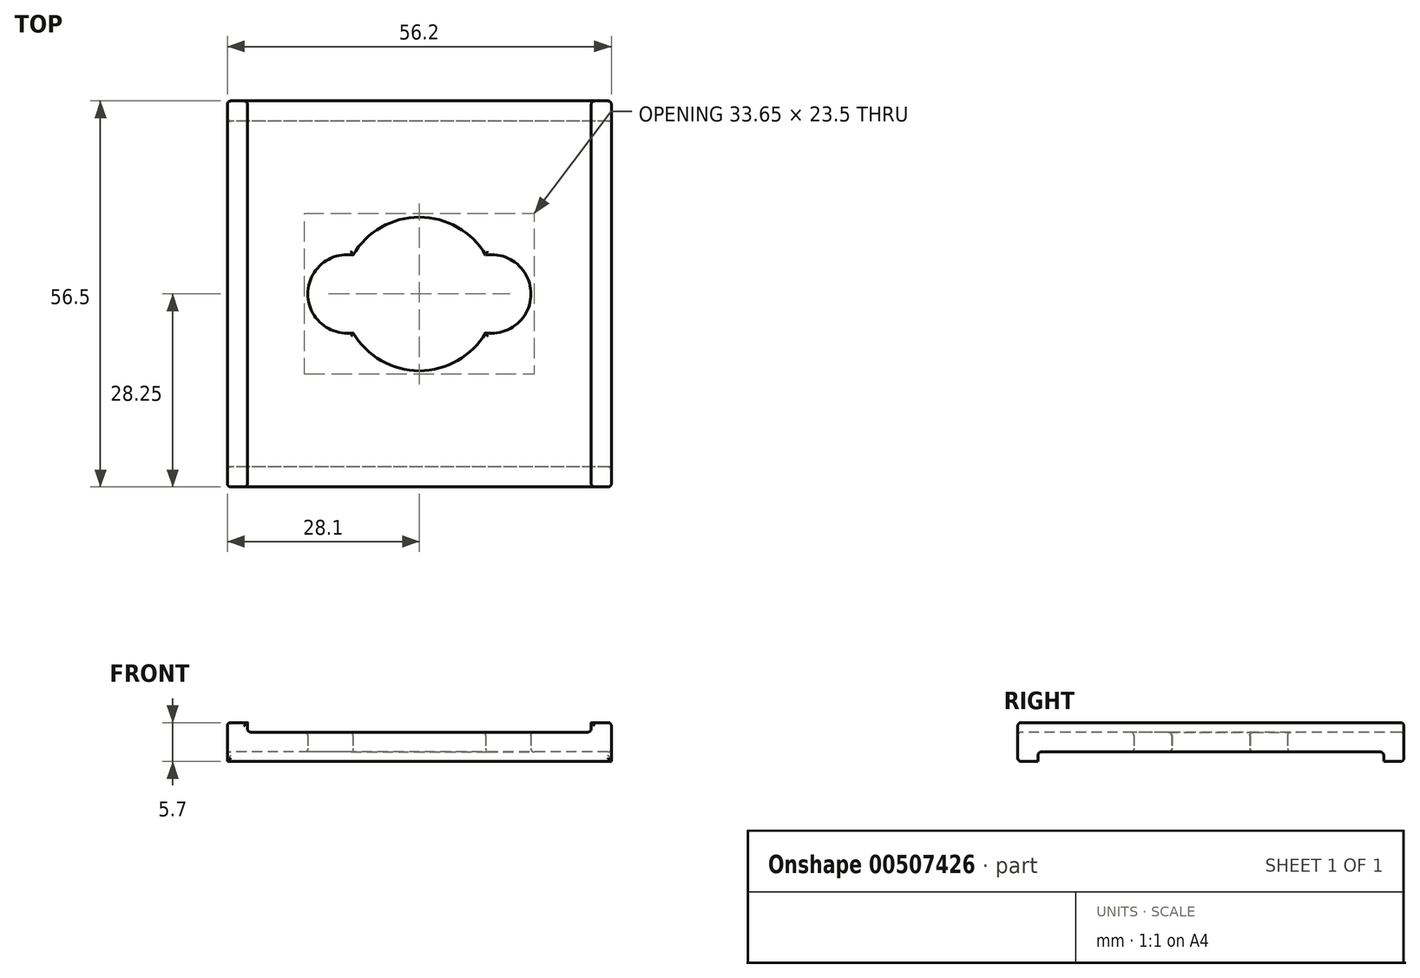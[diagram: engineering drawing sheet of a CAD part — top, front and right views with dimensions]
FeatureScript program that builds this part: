
annotation { "Feature Type Name" : "Feature", "Feature Type Description" : "" }
export const myFeature = defineFeature(function(context is Context, id is Id, definition is map)
    precondition{}
    {
        {
            var Q0;
            Q0=qCreatedBy(makeId("Top.planeOp"),FACE);
            var sketch = newSketch(context, id + "F0", { "sketchPlane" : qUnion([Q0])});
            skLineSegment(sketch, "E0.bottom", {"start": v(28.1, -28.25) * mm, "end": v(-28.1, -28.25) * mm});
            skLineSegment(sketch, "E0.top", {"start": v(28.1, 28.25) * mm, "end": v(-28.1, 28.25) * mm});
            skLineSegment(sketch, "E0.left", {"start": v(28.1, -28.25) * mm, "end": v(28.1, 28.25) * mm});
            skLineSegment(sketch, "E0.right", {"start": v(-28.1, -28.25) * mm, "end": v(-28.1, 28.25) * mm});
            skPoint(sketch, "E0.middle", {"position": v(0, 0) * mm});
            skSolve(sketch);
        }
        {
            var Q0;
            Q0 = qSketchRegion(id + "F0", true);
            extrude(context, id + "F1", {"entities" : qUnion([Q0]), "depth" : 2.9 * mm, "offsetDistance" : 25 * mm});
        }
        {
            var Q0;
            Q0=qCreatedBy(makeId("Top.planeOp"),FACE);
            var sketch = newSketch(context, id + "F2", { "sketchPlane" : qUnion([Q0])});
            skArc(sketch, "E1", {"start": v(9.7, 5.68) * mm, "mid": v(0, 11.25) * mm, "end": v(-9.7, 5.68) * mm});
            skArc(sketch, "E2", {"start": v(-9.7, 5.68) * mm, "mid": v(-16.32, 0) * mm, "end": v(-9.7, -5.68) * mm});
            skArc(sketch, "E3.MirrorC", {"start": v(9.7, 5.68) * mm, "mid": v(16.32, 0) * mm, "end": v(9.7, -5.68) * mm});
            skArc(sketch, "E4.trimOffspring", {"start": v(-9.7, -5.68) * mm, "mid": v(0, -11.25) * mm, "end": v(9.7, -5.68) * mm});
            skSolve(sketch);
        }
        {
            var Q0;
            Q0 = qSketchRegion(id + "F2", true);
            extrude(context, id + "F3", {"entities" : qUnion([Q0]), "operationType" : NewBodyOperationType.REMOVE, "endBound" : BoundingType.UP_TO_NEXT, "depth" : 25 * mm, "offsetDistance" : 25 * mm});
        }
        {
            var Q0;
            Q0=makeQuery(id+"F1.opExtrude","CAP_FACE",FACE,{"disambiguationData":[OSD([sQuery(id+"F0.wireOp",EDGE,"E0.bottom"),sQuery(id+"F0.wireOp",EDGE,"E0.top"),sQuery(id+"F0.wireOp",EDGE,"E0.left"),sQuery(id+"F0.wireOp",EDGE,"E0.right")])],"isStart":false});
            var sketch = newSketch(context, id + "F4", { "sketchPlane" : qUnion([Q0])});
            skLineSegment(sketch, "E5.bottom", {"start": v(-28.1, 28.25) * mm, "end": v(-25.15, 28.25) * mm});
            skLineSegment(sketch, "E5.top", {"start": v(-28.1, -28.25) * mm, "end": v(-25.15, -28.25) * mm});
            skLineSegment(sketch, "E5.left", {"start": v(-28.1, 28.25) * mm, "end": v(-28.1, -28.25) * mm});
            skLineSegment(sketch, "E5.right", {"start": v(-25.15, 28.25) * mm, "end": v(-25.15, -28.25) * mm});
            skLineSegment(sketch, "E6.MirrorCS", {"start": v(28.1, 28.25) * mm, "end": v(25.15, 28.25) * mm});
            skLineSegment(sketch, "E7.MirrorCS", {"start": v(28.1, -28.25) * mm, "end": v(25.15, -28.25) * mm});
            skLineSegment(sketch, "E8.MirrorCS", {"start": v(28.1, 28.25) * mm, "end": v(28.1, -28.25) * mm});
            skLineSegment(sketch, "E9.MirrorCS", {"start": v(25.15, 28.25) * mm, "end": v(25.15, -28.25) * mm});
            skSolve(sketch);
        }
        {
            var Q0;
            Q0 = qSketchRegion(id + "F4", true);
            extrude(context, id + "F5", {"entities" : qUnion([Q0]), "operationType" : NewBodyOperationType.ADD, "depth" : 1.4 * mm, "offsetDistance" : 25 * mm});
        }
        {
            var Q0;
            Q0=makeQuery(id+"F1.opExtrude","CAP_FACE",FACE,{"disambiguationData":[OSD([sQuery(id+"F0.wireOp",EDGE,"E0.bottom"),sQuery(id+"F0.wireOp",EDGE,"E0.top"),sQuery(id+"F0.wireOp",EDGE,"E0.left"),sQuery(id+"F0.wireOp",EDGE,"E0.right")])],"isStart":true});
            var sketch = newSketch(context, id + "F6", { "sketchPlane" : qUnion([Q0])});
            skLineSegment(sketch, "E10.bottom", {"start": v(28.1, -28.25) * mm, "end": v(-28.1, -28.25) * mm});
            skLineSegment(sketch, "E10.top", {"start": v(28.1, -25.3) * mm, "end": v(-28.1, -25.3) * mm});
            skLineSegment(sketch, "E10.left", {"start": v(28.1, -28.25) * mm, "end": v(28.1, -25.3) * mm});
            skLineSegment(sketch, "E10.right", {"start": v(-28.1, -28.25) * mm, "end": v(-28.1, -25.3) * mm});
            skLineSegment(sketch, "E11.MirrorCS", {"start": v(28.1, 28.25) * mm, "end": v(28.1, 25.3) * mm});
            skLineSegment(sketch, "E12.MirrorCS", {"start": v(-28.1, 28.25) * mm, "end": v(-28.1, 25.3) * mm});
            skLineSegment(sketch, "E13.MirrorCS", {"start": v(28.1, 25.3) * mm, "end": v(-28.1, 25.3) * mm});
            skLineSegment(sketch, "E14.MirrorCS", {"start": v(28.1, 28.25) * mm, "end": v(-28.1, 28.25) * mm});
            skSolve(sketch);
        }
        {
            var Q0;
            Q0 = qSketchRegion(id + "F6", true);
            extrude(context, id + "F7", {"entities" : qUnion([Q0]), "operationType" : NewBodyOperationType.ADD, "depth" : 1.4 * mm, "offsetDistance" : 25 * mm});
        }
        {
            var Q0;
            Q0=makeQuery(id+"F1.opExtrude","CAP_FACE",FACE,{"disambiguationData":[OSD([sQuery(id+"F0.wireOp",EDGE,"E0.bottom"),sQuery(id+"F0.wireOp",EDGE,"E0.top"),sQuery(id+"F0.wireOp",EDGE,"E0.left"),sQuery(id+"F0.wireOp",EDGE,"E0.right")])],"isStart":false});
            var Q1;
            Q1=makeQuery(id+"F1.opExtrude","CAP_FACE",FACE,{"disambiguationData":[OSD([sQuery(id+"F0.wireOp",EDGE,"E0.bottom"),sQuery(id+"F0.wireOp",EDGE,"E0.top"),sQuery(id+"F0.wireOp",EDGE,"E0.left"),sQuery(id+"F0.wireOp",EDGE,"E0.right")])],"isStart":true});
            var Q2;
            Q2=makeQuery(id+"F7.boolean.opBoolean","MERGE",FACE,{"derivedFrom":[makeQuery(id+"F5.boolean.opBoolean","MERGE",FACE,{"derivedFrom":[makeQuery(id+"F1.opExtrude","SWEPT_FACE",FACE,{"disambiguationData":[OSD([sQuery(id+"F0.wireOp",EDGE,"E0.top")])]}),makeQuery(id+"F5.opExtrude","SWEPT_FACE",FACE,{"disambiguationData":[OSD([sQuery(id+"F4.wireOp",EDGE,"E5.bottom")])]}),makeQuery(id+"F5.opExtrude","SWEPT_FACE",FACE,{"disambiguationData":[OSD([sQuery(id+"F4.wireOp",EDGE,"E6.MirrorCS")])]})]}),makeQuery(id+"F7.opExtrude","SWEPT_FACE",FACE,{"disambiguationData":[OSD([sQuery(id+"F6.wireOp",EDGE,"E10.bottom")])]})]});
            var Q3;
            Q3=makeQuery(id+"F7.boolean.opBoolean","MERGE",FACE,{"derivedFrom":[makeQuery(id+"F5.boolean.opBoolean","MERGE",FACE,{"derivedFrom":[makeQuery(id+"F1.opExtrude","SWEPT_FACE",FACE,{"disambiguationData":[OSD([sQuery(id+"F0.wireOp",EDGE,"E0.bottom")])]}),makeQuery(id+"F5.opExtrude","SWEPT_FACE",FACE,{"disambiguationData":[OSD([sQuery(id+"F4.wireOp",EDGE,"E5.top")])]}),makeQuery(id+"F5.opExtrude","SWEPT_FACE",FACE,{"disambiguationData":[OSD([sQuery(id+"F4.wireOp",EDGE,"E7.MirrorCS")])]})]}),makeQuery(id+"F7.opExtrude","SWEPT_FACE",FACE,{"disambiguationData":[OSD([sQuery(id+"F6.wireOp",EDGE,"E14.MirrorCS")])]})]});
            fillet(context, id + "F8", {"entities" : qUnion([Q0, Q1, Q2, Q3]), "radius" : 0.5 * mm, "tangentPropagation" : true, "allowEdgeOverflow" : false});
        }
        {
            var Q0;
            Q0=makeQuery(id+"F5.opExtrude","CAP_EDGE",EDGE,{"disambiguationData":[OSD([sQuery(id+"F4.wireOp",EDGE,"E8.MirrorCS")])],"isStart":false});
            var Q1;
            Q1=makeQuery(id+"F5.opExtrude","CAP_EDGE",EDGE,{"disambiguationData":[OSD([sQuery(id+"F4.wireOp",EDGE,"E5.left")])],"isStart":false});
            fillet(context, id + "F9", {"entities" : qUnion([Q0, Q1]), "radius" : 0.5 * mm, "tangentPropagation" : true, "allowEdgeOverflow" : false});
        }
    });
